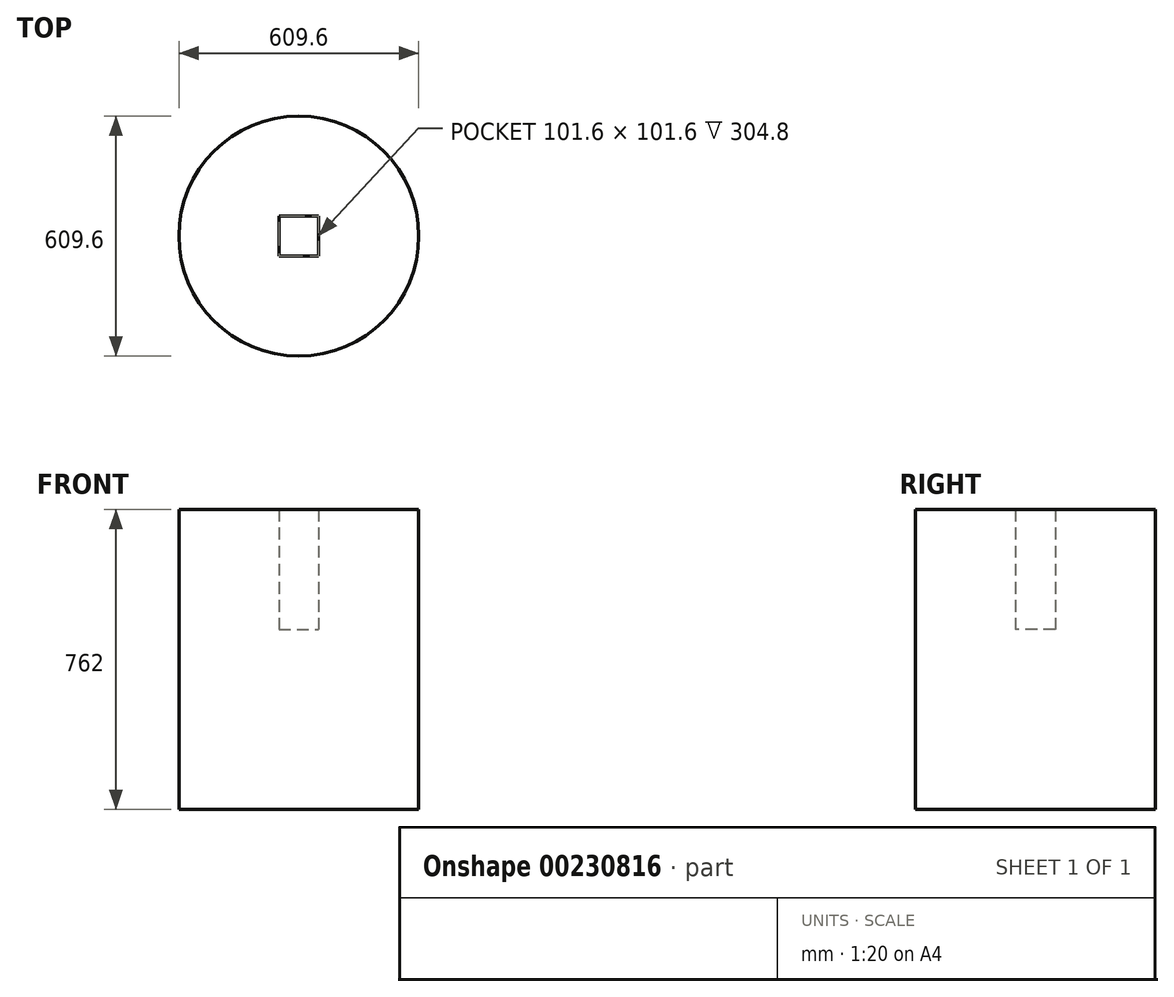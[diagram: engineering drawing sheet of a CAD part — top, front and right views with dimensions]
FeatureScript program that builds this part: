
annotation { "Feature Type Name" : "Feature", "Feature Type Description" : "" }
export const myFeature = defineFeature(function(context is Context, id is Id, definition is map)
    precondition{}
    {
        {
            var Q0;
            Q0=qCreatedBy(makeId("Top.planeOp"),FACE);
            var sketch = newSketch(context, id + "F0", { "sketchPlane" : qUnion([Q0])});
            skCircle(sketch, "E0", {"center": v(-73.6, 7.46) * mm, "radius": 304.8 * mm});
            skLineSegment(sketch, "E1.bottom", {"start": v(-124.4, 58.26) * mm, "end": v(-22.8, 58.26) * mm});
            skLineSegment(sketch, "E1.top", {"start": v(-124.4, -43.34) * mm, "end": v(-22.8, -43.34) * mm});
            skLineSegment(sketch, "E1.left", {"start": v(-124.4, 58.26) * mm, "end": v(-124.4, -43.34) * mm});
            skLineSegment(sketch, "E1.right", {"start": v(-22.8, 58.26) * mm, "end": v(-22.8, -43.34) * mm});
            skSolve(sketch);
        }
        {
            var Q0;
            Q0=makeQuery(id+"F0.imprint","IMPRINT",FACE,{"disambiguationData":[TD([[makeQuery(id+"F0.imprint","IMPRINT",EDGE,{"derivedFrom":sQuery(id+"F0.wireOp",EDGE,"E0")}),1.0]])]});
            extrude(context, id + "F1", {"entities" : qUnion([Q0]), "depth" : 762 * mm});
        }
        {
            var Q0;
            Q0=makeQuery(id+"F0.imprint","IMPRINT",FACE,{"disambiguationData":[TD([[makeQuery(id+"F0.imprint","IMPRINT",EDGE,{"derivedFrom":sQuery(id+"F0.wireOp",EDGE,"E1.bottom")}),-1.0]])]});
            extrude(context, id + "F2", {"entities" : qUnion([Q0]), "operationType" : NewBodyOperationType.ADD, "depth" : 457.2 * mm});
        }
    });
